FCSTD DOCUMENT  (FreeCAD 0.20R29177 +426 (Git))
Label: ASM_ExtensionHead
License: All rights reserved
LicenseURL: http://en.wikipedia.org/wiki/All_rights_reserved
objects: App::Link×6, App::DocumentObjectGroup×3, PartDesign::CoordinateSystem×1, App::FeaturePython×1, App::Part×1
note: 1 computed .brp shape members not serialized (recipe doc carries the construction recipe); baked Part::Feature solids carry a one-line shape summary decoded from their .brp
EXTERNAL_REF file=EndStopTip.FCStd obj=LCS_Origin
EXTERNAL_REF file=EndStopTip.FCStd obj=Assembly
EXTERNAL_REF file=BreakawayMagnet.FCStd obj=LCS_Origin
EXTERNAL_REF file=EndStopTip.FCStd obj=Variables
EXTERNAL_REF file=BreakawayMagnet.FCStd obj=Assembly
EXTERNAL_REF file=BreakawayHeadBase.FCStd obj=LCS_Origin
EXTERNAL_REF file=EndStopTip.FCStd obj=Pad
EXTERNAL_REF file=EndStopTip.FCStd obj=Pad001
EXTERNAL_REF file=BreakawayHeadBase.FCStd obj=Assembly
EXTERNAL_REF file=ASM_TrussPulley.FCStd obj=LCS_Origin
EXTERNAL_REF file=BreakawayHeadBase.FCStd obj=Sketch002
EXTERNAL_REF file=BreakawayHeadTruss.FCStd obj=Variables
EXTERNAL_REF file=ASM_TrussPulley.FCStd obj=Assembly
EXTERNAL_REF file=HeadTetherMountClip.FCStd obj=LCS_Origin
EXTERNAL_REF file=HeadTetherMountClip.FCStd obj=Assembly

FEATURE [App::DocumentObjectGroup] Parts
FEATURE [PartDesign::CoordinateSystem] LCS_Origin
  AttacherType = Attacher::AttachEngine3D
  MapMode = 2
  Support = -> [X_Axis]
FEATURE [App::FeaturePython] Variables  # WARN: FeaturePython — macro-defined, semantics opaque (R4)
  Type = App::PropertyContainer
FEATURE [App::DocumentObjectGroup] Constraints
FEATURE [App::DocumentObjectGroup] Configurations
FEATURE [App::Link] EndStopTip
  AttachedBy = #LCS_Origin
  AttachedTo = Parent Assembly#LCS_Origin
  AttachmentOffset = pos=(0,0,0) rot=(0,-0.707107,-0.707107;3.14159rad)
  LinkPlacement = pos=(0,0,0) rot=(0,-0.707107,-0.707107;3.14159rad)
  LinkedObject = -> <external EndStopTip.FCStd>#Assembly
  Placement = pos=(0,0,0) rot=(0,-0.707107,-0.707107;3.14159rad)
  SolverId = Asm4EE
  expr: Placement = LCS_Origin.Placement * AttachmentOffset * EndStopTip#LCS_Origin.Placement ^ -1
FEATURE [App::Link] BreakawayMagnet  label="BreakawayMagnetTop"
  AttachedBy = #LCS_Origin
  AttachedTo = EndStopTip#LCS_Origin
  AttachmentOffset = pos=(0,-10,5) rot=(0,0,1;0rad)
  LinkPlacement = pos=(-1.3e-15,5,-10) rot=(0,-0.707107,-0.707107;3.14159rad)
  LinkedObject = -> <external BreakawayMagnet.FCStd>#Assembly
  Placement = pos=(-1.3e-15,5,-10) rot=(0,-0.707107,-0.707107;3.14159rad)
  SolverId = Asm4EE
  expr: .AttachmentOffset.Base.z = <<EndStopTip>>#<<Variables>>.BaseHeight
  expr: Placement = EndStopTip.Placement * EndStopTip#LCS_Origin.Placement * AttachmentOffset * BreakawayMagnet#LCS_Origin.Placement ^ -1
FEATURE [App::Link] BreakawayMagnet001  label="BreakawayMagnetBottom"
  AttachedBy = #LCS_Origin
  AttachedTo = EndStopTip#LCS_Origin
  AttachmentOffset = pos=(0,10,5) rot=(0,0,1;0rad)
  LinkPlacement = pos=(4e-16,5,10) rot=(0,-0.707107,-0.707107;3.14159rad)
  LinkedObject = -> <external BreakawayMagnet.FCStd>#Assembly
  Placement = pos=(4e-16,5,10) rot=(0,-0.707107,-0.707107;3.14159rad)
  SolverId = Asm4EE
  expr: .AttachmentOffset.Base.z = <<EndStopTip>>#<<Variables>>.BaseHeight
  expr: Placement = EndStopTip.Placement * EndStopTip#LCS_Origin.Placement * AttachmentOffset * BreakawayMagnet#LCS_Origin.Placement ^ -1
FEATURE [App::Link] BreakawayHeadBase
  AttachedBy = #LCS_Origin
  AttachedTo = EndStopTip#LCS_Origin
  AttachmentOffset = pos=(0,0,10) rot=(0,-0.707107,0.707107;3.14159rad)
  LinkPlacement = pos=(-9e-16,10,-2.2e-15) rot=(-1,0,0;3.14159rad)
  LinkedObject = -> <external BreakawayHeadBase.FCStd>#Assembly
  Placement = pos=(-9e-16,10,-2.2e-15) rot=(-1,0,0;3.14159rad)
  SolverId = Asm4EE
  expr: .AttachmentOffset.Base.z = <<EndStopTip>>#<<Pad>>.Length + <<EndStopTip>>#<<MagnetPad>>.Length
  expr: Placement = EndStopTip.Placement * EndStopTip#LCS_Origin.Placement * AttachmentOffset * BreakawayHeadBase#LCS_Origin.Placement ^ -1
FEATURE [App::Link] ASM_TrussPulley
  AttachedBy = #LCS_Origin
  AttachedTo = BreakawayHeadBase#LCS_Origin
  AttachmentOffset = pos=(0,-18,-16) rot=(1,0,0;3.40339rad)
  LinkPlacement = pos=(-4e-15,28,16) rot=(1,0,0;0.261799rad)
  LinkedObject = -> <external ASM_TrussPulley.FCStd>#Assembly
  Placement = pos=(-4e-15,28,16) rot=(1,0,0;0.261799rad)
  SolverId = Asm4EE
  expr: .AttachmentOffset.Base.y = <<BreakawayHeadBase>>#<<Sketch002>>.Constraints.HolesOffset * -1
  expr: .AttachmentOffset.Base.z = <<BreakawayHeadBase>>#<<Sketch002>>.Constraints.TrussHoleSpacing / -2
  expr: .AttachmentOffset.Rotation.Angle = 180 + <<BreakawayHeadTruss>>#<<Variables>>.TrussAngle
  expr: Placement = BreakawayHeadBase.Placement * BreakawayHeadBase#LCS_Origin.Placement * AttachmentOffset * ASM_TrussPulley#LCS_Origin.Placement ^ -1
FEATURE [App::Link] HeadTetherMountClip
  AttachedBy = #LCS_Origin
  AttachedTo = Parent Assembly#LCS_Origin
  AttachmentOffset = pos=(10,-18,-10) rot=(0.57735,0.57735,0.57735;2.0944rad)
  LinkPlacement = pos=(10,-18,-10) rot=(0.57735,0.57735,0.57735;2.0944rad)
  LinkedObject = -> <external HeadTetherMountClip.FCStd>#Assembly
  Placement = pos=(10,-18,-10) rot=(0.57735,0.57735,0.57735;2.0944rad)
  SolverId = Asm4EE
  expr: Placement = LCS_Origin.Placement * AttachmentOffset * HeadTetherMountClip#LCS_Origin.Placement ^ -1
FEATURE [App::Part] Assembly
  AssemblyType = Part::Link
  Group = -> [LCS_Origin,Variables,Constraints,Configurations,EndStopTip,BreakawayMagnet,BreakawayMagnet001,BreakawayHeadBase,ASM_TrussPulley,HeadTetherMountClip]
  Origin = -> Origin
  Type = Assembly

RESOLVED EXTERNAL PARTS (link-assembly join: the EXTERNAL_REF files above that resolve inside this repo's crawl, each included once):
---- part ASM_TrussPulley.FCStd = doc fcstd_1721cb35d806 ----
FCSTD DOCUMENT  (FreeCAD 0.20R29177 +426 (Git))
Label: ASM_TrussPulley
License: All rights reserved
LicenseURL: http://en.wikipedia.org/wiki/All_rights_reserved
objects: App::Link×7, App::DocumentObjectGroup×3, PartDesign::CoordinateSystem×2, App::FeaturePython×1, App::Part×1
note: 2 computed .brp shape members not serialized (recipe doc carries the construction recipe); baked Part::Feature solids carry a one-line shape summary decoded from their .brp
EXTERNAL_REF file=BreakawayHeadBase.FCStd obj=Sketch
EXTERNAL_REF file=BreakawayHeadTruss.FCStd obj=LCS_Origin
EXTERNAL_REF file=BreakawayHeadTruss.FCStd obj=Assembly
EXTERNAL_REF file=BreakawayHeadTruss.FCStd obj=Pad
EXTERNAL_REF file=BreakawayHeadTruss.FCStd obj=Sketch
EXTERNAL_REF file=CablePulley.FCStd obj=LCS_Origin
EXTERNAL_REF file=CablePulley.FCStd obj=Assembly
EXTERNAL_REF file=Bearing608.FCStd obj=LCS_axle
EXTERNAL_REF file=Bearing608.FCStd obj=Part
EXTERNAL_REF file=CablePulleyBearingHub.FCStd obj=LCS_Origin
EXTERNAL_REF file=CablePulleyBearingHub.FCStd obj=Assembly

FEATURE [App::DocumentObjectGroup] Parts
FEATURE [PartDesign::CoordinateSystem] LCS_Origin
  AttacherType = Attacher::AttachEngine3D
  MapMode = 2
  Support = -> [X_Axis]
FEATURE [App::FeaturePython] Variables  # WARN: FeaturePython — macro-defined, semantics opaque (R4)
  Type = App::PropertyContainer
FEATURE [App::DocumentObjectGroup] Constraints
FEATURE [App::DocumentObjectGroup] Configurations
FEATURE [App::Link] BreakawayHeadTruss
  AttachedBy = #LCS_Origin
  AttachedTo = Parent Assembly#LCS_Origin
  AttachmentOffset = pos=(8,0,0) rot=(0.57735,0.57735,0.57735;2.0944rad)
  LinkPlacement = pos=(8,0,0) rot=(0.57735,0.57735,0.57735;2.0944rad)
  LinkedObject = -> <external BreakawayHeadTruss.FCStd>#Assembly
  Placement = pos=(8,0,0) rot=(0.57735,0.57735,0.57735;2.0944rad)
  SolverId = Asm4EE
  expr: .AttachmentOffset.Base.x = <<BreakawayHeadBase>>#<<Sketch>>.Constraints.EndWidth / 2
  expr: Placement = LCS_Origin.Placement * AttachmentOffset * BreakawayHeadTruss#LCS_Origin.Placement ^ -1
FEATURE [App::Link] BreakawayHeadTruss001
  AttachedBy = #LCS_Origin
  AttachedTo = Parent Assembly#LCS_Origin
  AttachmentOffset = pos=(-10,0,0) rot=(0.57735,0.57735,0.57735;2.0944rad)
  LinkPlacement = pos=(-10,0,0) rot=(0.57735,0.57735,0.57735;2.0944rad)
  LinkedObject = -> <external BreakawayHeadTruss.FCStd>#Assembly
  Placement = pos=(-10,0,0) rot=(0.57735,0.57735,0.57735;2.0944rad)
  SolverId = Asm4EE
  expr: .AttachmentOffset.Base.x = (<<BreakawayHeadBase>>#<<Sketch>>.Constraints.EndWidth / 2 + <<BreakawayHeadTruss>>#<<Pad>>.Length) * -1
  expr: Placement = LCS_Origin.Placement * AttachmentOffset * BreakawayHeadTruss#LCS_Origin.Placement ^ -1
FEATURE [PartDesign::CoordinateSystem] LCS_Pulley
  AttacherType = Attacher::AttachEngine3D
  AttachmentOffset = pos=(0,180,-29.9096) rot=(0,0,1;0rad)
  MapMode = 2
  Placement = pos=(0,180,-29.9096) rot=(0,0,1;0rad)
  Support = -> [LCS_Origin]
  expr: .AttachmentOffset.Base.y = BreakawayHeadTruss#Sketch.Constraints.TrussLength
  expr: .AttachmentOffset.Base.z = BreakawayHeadTruss#Sketch.Constraints.PulleyHoleOffset * -1
FEATURE [App::Link] CablePulley
  AttachedBy = #LCS_Origin
  AttachedTo = Parent Assembly#LCS_Pulley
  AttachmentOffset = pos=(0,0,0) rot=(0,1,0;1.5708rad)
  LinkPlacement = pos=(0,180,-29.9096) rot=(0,1,0;1.5708rad)
  LinkedObject = -> <external CablePulley.FCStd>#Assembly
  Placement = pos=(0,180,-29.9096) rot=(0,1,0;1.5708rad)
  SolverId = Asm4EE
  expr: Placement = LCS_Pulley.Placement * AttachmentOffset * CablePulley#LCS_Origin.Placement ^ -1
FEATURE [App::Link] PulleyBearing
  AssemblyType = Part::Link
  AttachedBy = #LCS_axle
  AttachedTo = Parent Assembly#LCS_Pulley
  AttachmentOffset = pos=(0,0,0) rot=(0,1,0;1.5708rad)
  LinkPlacement = pos=(0,180,-29.9096) rot=(0,1,0;1.5708rad)
  LinkedObject = -> <external Bearing608.FCStd>#Part
  Placement = pos=(0,180,-29.9096) rot=(0,1,0;1.5708rad)
  SolverId = Asm4EE
  expr: Placement = LCS_Pulley.Placement * AttachmentOffset * Bearing608#LCS_axle.Placement ^ -1
FEATURE [App::Link] CablePulleyBearingHub001
  AttachedBy = #LCS_Origin
  AttachedTo = Parent Assembly#LCS_Pulley
  AttachmentOffset = pos=(3.5,0,0) rot=(0,1,0;4.71239rad)
  LinkPlacement = pos=(3.5,180,-29.9096) rot=(0,1,0;4.71239rad)
  LinkedObject = -> <external CablePulleyBearingHub.FCStd>#Assembly
  Placement = pos=(3.5,180,-29.9096) rot=(0,1,0;4.71239rad)
  SolverId = Asm4EE
  expr: Placement = LCS_Pulley.Placement * AttachmentOffset * CablePulleyBearingHub#LCS_Origin.Placement ^ -1
FEATURE [App::Link] CablePulleyBearingHub002
  AttachedBy = #LCS_Origin
  AttachedTo = Parent Assembly#LCS_Pulley
  AttachmentOffset = pos=(-3.5,0,0) rot=(-0.707107,0,-0.707107;3.14159rad)
  LinkPlacement = pos=(-3.5,180,-29.9096) rot=(-0.707107,0,-0.707107;3.14159rad)
  LinkedObject = -> <external CablePulleyBearingHub.FCStd>#Assembly
  Placement = pos=(-3.5,180,-29.9096) rot=(-0.707107,0,-0.707107;3.14159rad)
  SolverId = Asm4EE
  expr: Placement = LCS_Pulley.Placement * AttachmentOffset * CablePulleyBearingHub#LCS_Origin.Placement ^ -1
FEATURE [App::Link] CablePulley001
  AttachedBy = #LCS_Origin
  AttachedTo = Parent Assembly#LCS_Pulley
  AttachmentOffset = pos=(0,0,0) rot=(0,1,0;-1.5708rad)
  LinkPlacement = pos=(0,180,-29.9096) rot=(0,1,0;4.71239rad)
  LinkedObject = -> <external CablePulley.FCStd>#Assembly
  Placement = pos=(0,180,-29.9096) rot=(0,1,0;4.71239rad)
  SolverId = Asm4EE
  expr: Placement = LCS_Pulley.Placement * AttachmentOffset * CablePulley#LCS_Origin.Placement ^ -1
FEATURE [App::Part] Assembly
  AssemblyType = Part::Link
  Group = -> [LCS_Origin,Variables,Constraints,Configurations,BreakawayHeadTruss,BreakawayHeadTruss001,LCS_Pulley,CablePulley,PulleyBearing,CablePulleyBearingHub001,CablePulleyBearingHub002,CablePulley001]
  Origin = -> Origin
  Type = Assembly
---- part BreakawayHeadBase.FCStd = doc fcstd_181b5c8611f0 ----
FCSTD DOCUMENT  (FreeCAD 0.20R29177 +426 (Git))
Label: BreakawayHeadBase
License: All rights reserved
LicenseURL: http://en.wikipedia.org/wiki/All_rights_reserved
objects: Sketcher::SketchObject×5, App::DocumentObjectGroup×4, PartDesign::Pocket×4, Part::FeaturePython×4, PartDesign::CoordinateSystem×2, App::Link×2, App::FeaturePython×1, PartDesign::Pad×1, PartDesign::Body×1, App::Part×1
note: 22 computed .brp shape members not serialized (recipe doc carries the construction recipe); baked Part::Feature solids carry a one-line shape summary decoded from their .brp
EXTERNAL_REF file=EndStopTip.FCStd obj=Sketch003
EXTERNAL_REF file=EndStopTip.FCStd obj=Sketch
EXTERNAL_REF file=BreakawayMagnet.FCStd obj=LCS_Origin
EXTERNAL_REF file=BreakawayMagnet.FCStd obj=Assembly

FEATURE [App::DocumentObjectGroup] Parts
FEATURE [PartDesign::CoordinateSystem] LCS_Origin
  AttacherType = Attacher::AttachEngine3D
  MapMode = 2
  Support = -> [X_Axis]
FEATURE [App::FeaturePython] Variables  # WARN: FeaturePython — macro-defined, semantics opaque (R4)
  Type = App::PropertyContainer
FEATURE [App::DocumentObjectGroup] Constraints
FEATURE [App::DocumentObjectGroup] Configurations
FEATURE [Sketcher::SketchObject] Sketch
  FullyConstrained = true
  MapMode = 5
  Support = -> [XY_Plane001]
  expr: Constraints[9] = <<EndStopTip>>#<<SketchChamfer>>.Constraints.MateWidth
  sketch-geometry (14):
    g0: ArcOfCircle CenterX=-10.567 CenterY=-0.5 CenterZ=0 NormalX=0 NormalY=0 NormalZ=1 AngleXU=0 Radius=0.5 StartAngle=1.5708 EndAngle=3.66519
    g1: LineSegment StartX=-10.567 StartY=0 StartZ=0 EndX=10.567 EndY=0 EndZ=0
    g2: ArcOfCircle CenterX=10.567 CenterY=-0.5 CenterZ=0 NormalX=0 NormalY=0 NormalZ=1 AngleXU=0 Radius=0.5 StartAngle=5.75959 EndAngle=7.85398
    g3: LineSegment StartX=11 StartY=-0.75 StartZ=0 EndX=8 EndY=-5.94615 EndZ=0
    g4: LineSegment StartX=-8 StartY=-5.94615 StartZ=0 EndX=-11 EndY=-0.75 EndZ=0
    g5: GeomPoint X=-11.433 Y=0 Z=0
    g6: LineSegment StartX=-8 StartY=-5.94615 StartZ=0 EndX=-8 EndY=-23 EndZ=0
    g7: LineSegment StartX=-7 StartY=-24 StartZ=0 EndX=7 EndY=-24 EndZ=0
    g8: LineSegment StartX=8 StartY=-23 StartZ=0 EndX=8 EndY=-5.94615 EndZ=0
    g9: GeomPoint X=0 Y=-24 Z=0
    g10: ArcOfCircle CenterX=7 CenterY=-23 CenterZ=0 NormalX=0 NormalY=0 NormalZ=1 AngleXU=0 Radius=1 StartAngle=4.71239 EndAngle=6.28319
    g11: GeomPoint X=8 Y=-24 Z=0
    g12: ArcOfCircle CenterX=-7 CenterY=-23 CenterZ=0 NormalX=0 NormalY=0 NormalZ=1 AngleXU=0 Radius=1 StartAngle=3.14159 EndAngle=4.71239
    g13: GeomPoint X=-8 Y=-24 Z=0
  constraints (32):
    c: Tangent(g0,g1) = 1.5708
    c: Tangent(g1,g2) = 1.5708
    c: Tangent(g2,g3) = 1.5708
    c: Tangent(g4,g0) = 1.5708
    c: Horizontal(g1)
    c: Equal(g0,g2)
    c: PointOnObject(g5,g1)
    c: PointOnObject(g5,g4)
    c: Radius(g0) = 0.5
    c: DistanceX(g0,g2) = 22
    c: Symmetric(g1,g0,g-1)
    c: Vertical(g6)
    c: Horizontal(g7)
    c: Vertical(g8)
    c: Symmetric(g13,g11,g9)
    c: PointOnObject(g9,g-2)
    c: Coincident(g4,g6)
    c: Coincident(g8,g3)
    c: Equal(g4,g3)
    c: Angle(g1,g3) = 1.0472
    c: DistanceX(g13,g11) = 16  'EndWidth'
    c: DistanceY(g11,g-1) = 24  'Length'
    c: PointOnObject(g11,g8)
    c: PointOnObject(g11,g7)
    c: Tangent(g8,g10) = -1.5708
    c: Tangent(g7,g10) = -1.5708
    c: PointOnObject(g13,g7)
    c: PointOnObject(g13,g6)
    c: Tangent(g7,g12) = -1.5708
    c: Tangent(g6,g12) = -1.5708
    c: Equal(g12,g10)
    c: Radius(g10) = 1
FEATURE [PartDesign::Pad] Pad
  Direction = (0,0,1)
  Length = 42
  Length2 = 10
  Midplane = true
  Profile = -> Sketch
  ReferenceAxis = -> Sketch [N_Axis]
  Type = 0
  expr: Length = <<EndStopTip>>#<<Sketch>>.Constraints.Height
FEATURE [Sketcher::SketchObject] Sketch001
  FullyConstrained = true
  MapMode = 5
  Placement = pos=(0,0,0) rot=(0.57735,0.57735,0.57735;2.0944rad)
  Support = -> [YZ_Plane001]
  expr: Constraints[25] = <<Sketch>>.Constraints.Length
  sketch-geometry (9):
    g0: LineSegment StartX=-24 StartY=13 StartZ=0 EndX=-34.7696 EndY=13 EndZ=0
    g1: LineSegment StartX=-34.7696 StartY=13 StartZ=0 EndX=-42.3848 EndY=5.38478 EndZ=0
    g2: LineSegment StartX=-42.3848 StartY=5.38478 StartZ=0 EndX=-42.3848 EndY=-5.38478 EndZ=0
    g3: LineSegment StartX=-42.3848 StartY=-5.38478 StartZ=0 EndX=-34.7696 EndY=-13 EndZ=0
    g4: LineSegment StartX=-34.7696 StartY=-13 StartZ=0 EndX=-24 EndY=-13 EndZ=0
    g5: LineSegment StartX=-24 StartY=-13 StartZ=0 EndX=-16.3848 EndY=-5.38478 EndZ=0
    g6: LineSegment StartX=-16.3848 StartY=-5.38478 StartZ=0 EndX=-16.3848 EndY=5.38478 EndZ=0
    g7: LineSegment StartX=-16.3848 StartY=5.38478 StartZ=0 EndX=-24 EndY=13 EndZ=0
    g8: Circle CenterX=-29.3848 CenterY=0 CenterZ=0 NormalX=0 NormalY=0 NormalZ=1 AngleXU=0 Radius=14.0711
  constraints (21):
    c: Coincident(g0,g1)
    c: Coincident(g1,g2)
    c: Coincident(g2,g3)
    c: Coincident(g3,g4)
    c: Coincident(g4,g5)
    c: Coincident(g5,g6)
    c: Coincident(g6,g7)
    c: Coincident(g7,g0)
    c: Equal(g0, g1-g7) x7
    c: PointOnObject(g0,g8)
    c: PointOnObject(g1,g8)
    c: PointOnObject(g2,g8)
    c: PointOnObject(g3,g8)
    c: PointOnObject(g4,g8)
    c: PointOnObject(g5,g8)
    c: PointOnObject(g6,g8)
    c: PointOnObject(g7,g8)
    c: PointOnObject(g8,g-1)
    c: Horizontal(g0)
    c: DistanceX(g4,g-1) = 24
    c: DistanceY(g3,g0) = 26
FEATURE [PartDesign::Pocket] Pocket  label="Cutout"
  BaseFeature = -> Pad
  Direction = (-1,2e-16,-3e-16)
  Length = 5
  Length2 = 5
  Midplane = true
  Profile = -> Sketch001
  ReferenceAxis = -> Sketch001 [N_Axis]
  Type = 1
FEATURE [Sketcher::SketchObject] Sketch002
  FullyConstrained = true
  MapMode = 5
  Placement = pos=(0,0,0) rot=(0.57735,0.57735,0.57735;2.0944rad)
  Support = -> [YZ_Plane001]
  expr: .Constraints.HolesOffset = <<Sketch>>.Constraints.Length - 6mm
  expr: .Constraints.TrussHoleSpacing = <<Pad>>.Length - 10mm
  sketch-geometry (12):
    g0: LineSegment StartX=-18 StartY=16 StartZ=0 EndX=-18 EndY=-16 EndZ=0
    g1: GeomPoint X=-18 Y=0 Z=0
    g2: ArcOfCircle CenterX=-18 CenterY=16 CenterZ=0 NormalX=0 NormalY=0 NormalZ=1 AngleXU=0 Radius=2.15 StartAngle=2.35619 EndAngle=7.06858
    g3: LineSegment StartX=-19.5203 StartY=17.5203 StartZ=0 EndX=-18.8906 EndY=18.15 EndZ=0
    g4: LineSegment StartX=-16.4797 StartY=17.5203 StartZ=0 EndX=-17.1094 EndY=18.15 EndZ=0
    g5: LineSegment StartX=-17.1094 StartY=18.15 StartZ=0 EndX=-18.8906 EndY=18.15 EndZ=0
    g6: ArcOfCircle CenterX=-18 CenterY=16 CenterZ=0 NormalX=0 NormalY=0 NormalZ=1 AngleXU=0 Radius=2.15 StartAngle=0.785398 EndAngle=2.35619
    g7: ArcOfCircle CenterX=-18 CenterY=-16 CenterZ=0 NormalX=0 NormalY=0 NormalZ=1 AngleXU=0 Radius=2.15 StartAngle=2.35619 EndAngle=7.06858
    g8: LineSegment StartX=-19.5203 StartY=-14.4797 StartZ=0 EndX=-18.8906 EndY=-13.85 EndZ=0
    g9: LineSegment StartX=-16.4797 StartY=-14.4797 StartZ=0 EndX=-17.1094 EndY=-13.85 EndZ=0
    g10: LineSegment StartX=-17.1094 StartY=-13.85 StartZ=0 EndX=-18.8906 EndY=-13.85 EndZ=0
    g11: ArcOfCircle CenterX=-18 CenterY=-16 CenterZ=0 NormalX=0 NormalY=0 NormalZ=1 AngleXU=0 Radius=2.15 StartAngle=0.785398 EndAngle=2.35619
  constraints (31):
    c: Vertical(g0)
    c: PointOnObject(g1,g-1)
    c: DistanceY(g0,g0) = 32  'TrussHoleSpacing'
    c: DistanceX(g1,g-1) = 18  'HolesOffset'
    c: Coincident(g2,g0)
    c: Symmetric(g2,g0,g1)
    c: Coincident(g5,g4)
    c: Coincident(g5,g3)
    c: Horizontal(g5)
    c: Tangent(g4,g2) = -1.5708
    c: Tangent(g3,g2) = 1.5708
    c: Diameter(g2) = 4.3
    c: Coincident(g6,g2)
    c: Coincident(g6,g2)
    c: Coincident(g6,g2)
    c: Tangent(g5,g6)
    c: Equal(g4,g3)
    c: Angle(g5,g4) = 2.35619
    c: Coincident(g10,g9)
    c: Coincident(g10,g8)
    c: Horizontal(g10)
    c: Tangent(g9,g7) = -1.5708
    c: Tangent(g8,g7) = 1.5708
    c: Equal(g2,g7) = 5.4
    c: Coincident(g11,g7)
    c: Coincident(g11,g7)
    c: Coincident(g11,g7)
    c: Tangent(g10,g11)
    c: Equal(g9,g8)
    c: Angle(g10,g9) = 2.35619
    c: Coincident(g7,g0)
FEATURE [PartDesign::Pocket] Pocket001  label="TrussHoles"
  BaseFeature = -> Pocket
  Direction = (-1,2e-16,-3e-16)
  Length = 5
  Length2 = 5
  Midplane = true
  Profile = -> Sketch002
  ReferenceAxis = -> Sketch002 [N_Axis]
  Type = 1
FEATURE [Sketcher::SketchObject] Sketch003
  FullyConstrained = true
  MapMode = 5
  Placement = pos=(0,0,0) rot=(1,0,0;1.5708rad)
  Support = -> [XZ_Plane001]
  sketch-geometry (13):
    g0: ArcOfCircle CenterX=0 CenterY=10 CenterZ=0 NormalX=0 NormalY=0 NormalZ=1 AngleXU=0 Radius=9.25 StartAngle=2.35619 EndAngle=3.92699
    g1: ArcOfCircle CenterX=0 CenterY=10 CenterZ=0 NormalX=0 NormalY=0 NormalZ=1 AngleXU=0 Radius=9.25 StartAngle=5.49779 EndAngle=7.06858
    g2: ArcOfCircle CenterX=-9e-16 CenterY=-10 CenterZ=0 NormalX=0 NormalY=0 NormalZ=1 AngleXU=0 Radius=9.25 StartAngle=5.49779 EndAngle=7.06858
    g3: ArcOfCircle CenterX=-9e-16 CenterY=-10 CenterZ=0 NormalX=0 NormalY=0 NormalZ=1 AngleXU=0 Radius=9.25 StartAngle=2.35619 EndAngle=3.92699
    g4: LineSegment StartX=-6.54074 StartY=3.45926 StartZ=0 EndX=-6.54074 EndY=-3.45926 EndZ=0
    g5: LineSegment StartX=6.54074 StartY=3.45926 StartZ=0 EndX=6.54074 EndY=-3.45926 EndZ=0
    g6: LineSegment StartX=6.54074 StartY=-16.5407 StartZ=0 EndX=6.54074 EndY=-22.5407 EndZ=0
    g7: LineSegment StartX=6.54074 StartY=-22.5407 StartZ=0 EndX=-6.54074 EndY=-22.5407 EndZ=0
    g8: LineSegment StartX=-6.54074 StartY=-22.5407 StartZ=0 EndX=-6.54074 EndY=-16.5407 EndZ=0
    g9: LineSegment StartX=-6.54074 StartY=16.5407 StartZ=0 EndX=-6.54074 EndY=22.5407 EndZ=0
    g10: LineSegment StartX=-6.54074 StartY=22.5407 StartZ=0 EndX=6.54074 EndY=22.5407 EndZ=0
    g11: LineSegment StartX=6.54074 StartY=22.5407 StartZ=0 EndX=6.54074 EndY=16.5407 EndZ=0
    g12: LineSegment StartX=-6.54074 StartY=-3.45926 StartZ=0 EndX=-3.08148 EndY=0 EndZ=0
  constraints (39):
    c: PointOnObject(g1,g-2)
    c: Symmetric(g1,g3,g-1)
    c: DistanceY(g3,g1) = 20
    c: Coincident(g1,g0)
    c: Diameter(g1) = 18.5
    c: Coincident(g3,g2)
    c: Coincident(g4,g0)
    c: Coincident(g4,g3)
    c: Coincident(g5,g1)
    c: Coincident(g5,g2)
    c: Coincident(g6,g2)
    c: Vertical(g6)
    c: Coincident(g7,g6)
    c: Horizontal(g7)
    c: Coincident(g8,g3)
    c: Vertical(g8)
    c: Coincident(g9,g0)
    c: Vertical(g9)
    c: Coincident(g10,g9)
    c: Horizontal(g10)
    c: Coincident(g11,g10)
    c: Coincident(g11,g1)
    c: Vertical(g11)
    c: Vertical(g5)
    c: Vertical(g4)
    c: Equal(g0,g1)
    c: Equal(g2,g3)
    c: Equal(g2,g1)
    c: Equal(g6,g8)
    c: Coincident(g8,g7)
    c: Equal(g9,g11)
    c: Equal(g10,g7)
    c: PointOnObject(g2,g6)
    c: PointOnObject(g3,g8)
    c: PointOnObject(g12,g-1)
    c: Tangent(g12,g3) = 1.5708
    c: Angle(g12,g-1) = 2.35619
    c: DistanceY(g11,g11) = 6
    c: Equal(g6,g11)
FEATURE [PartDesign::Pocket] Pocket002  label="MagnetHoles"
  BaseFeature = -> Pocket001
  Direction = (0,1,2e-16)
  Length = 1.5
  Length2 = 5
  Profile = -> Sketch003
  ReferenceAxis = -> Sketch003 [N_Axis]
  Reversed = true
  Type = 0
FEATURE [Sketcher::SketchObject] Sketch004
  FullyConstrained = true
  MapMode = 5
  Placement = pos=(0,0,0) rot=(1,0,0;1.5708rad)
  Support = -> [XZ_Plane001]
  sketch-geometry (8):
    g0: ArcOfCircle CenterX=0 CenterY=10 CenterZ=0 NormalX=0 NormalY=0 NormalZ=1 AngleXU=0 Radius=2.25 StartAngle=2.35619 EndAngle=7.06858
    g1: LineSegment StartX=-1.59099 StartY=11.591 StartZ=0 EndX=-0.931981 EndY=12.25 EndZ=0
    g2: LineSegment StartX=-0.931981 StartY=12.25 StartZ=0 EndX=0.931981 EndY=12.25 EndZ=0
    g3: LineSegment StartX=0.931981 StartY=12.25 StartZ=0 EndX=1.59099 EndY=11.591 EndZ=0
    g4: ArcOfCircle CenterX=0 CenterY=-10 CenterZ=0 NormalX=0 NormalY=0 NormalZ=1 AngleXU=0 Radius=2.25 StartAngle=2.35619 EndAngle=7.06858
    g5: LineSegment StartX=-1.59099 StartY=-8.40901 StartZ=0 EndX=-0.931981 EndY=-7.75 EndZ=0
    g6: LineSegment StartX=-0.931981 StartY=-7.75 StartZ=0 EndX=0.931981 EndY=-7.75 EndZ=0
    g7: LineSegment StartX=0.931981 StartY=-7.75 StartZ=0 EndX=1.59099 EndY=-8.40901 EndZ=0
  constraints (21):
    c: PointOnObject(g0,g-2)
    c: Coincident(g2,g1)
    c: Horizontal(g2)
    c: Coincident(g3,g2)
    c: Tangent(g3,g0) = 1.5708
    c: Tangent(g1,g0) = 1.5708
    c: Equal(g1,g3)
    c: Angle(g2,g3) = 2.35619
    c: Diameter(g0) = 4.5
    c: Tangent(g2,g0)
    c: Coincident(g6,g5)
    c: Horizontal(g6)
    c: Coincident(g7,g6)
    c: Tangent(g7,g4) = 1.5708
    c: Tangent(g5,g4) = 1.5708
    c: Equal(g5,g7)
    c: Angle(g6,g7) = 2.35619
    c: Equal(g0,g4) = 4.5
    c: Tangent(g6,g4)
    c: Symmetric(g4,g0,g-1)
    c: DistanceY(g4,g0) = 20
FEATURE [PartDesign::Pocket] Pocket003  label="MagnetMountHoles"
  BaseFeature = -> Pocket002
  Direction = (0,1,2e-16)
  Length = 16
  Length2 = 5
  Profile = -> Sketch004
  ReferenceAxis = -> Sketch004 [N_Axis]
  Reversed = true
  Type = 0
FEATURE [PartDesign::Body] Body
  Group = -> [Sketch,Pad,Sketch001,Pocket,Sketch002,Pocket001,Sketch003,Pocket002,Sketch004,Pocket003]
  Origin = -> Origin001
  Tip = -> Pocket003
FEATURE [App::Link] BreakawayMagnetTop
  AttachedBy = #LCS_Origin
  AttachedTo = Parent Assembly#LCS_Origin
  AttachmentOffset = pos=(0,-1.5,10) rot=(1,0,0;4.71239rad)
  LinkPlacement = pos=(0,-1.5,10) rot=(1,0,0;4.71239rad)
  LinkedObject = -> <external BreakawayMagnet.FCStd>#Assembly
  Placement = pos=(0,-1.5,10) rot=(1,0,0;4.71239rad)
  SolverId = Asm4EE
  expr: .AttachmentOffset.Base.y = <<MagnetHoles>>.Length * -1
  expr: Placement = LCS_Origin.Placement * AttachmentOffset * BreakawayMagnet#LCS_Origin.Placement ^ -1
FEATURE [App::Link] BreakawayMagnetTop001  label="BreakawayMagnetBottom"
  AttachedBy = #LCS_Origin
  AttachedTo = Parent Assembly#LCS_Origin
  AttachmentOffset = pos=(0,-1.5,-10) rot=(1,0,0;4.71239rad)
  LinkPlacement = pos=(0,-1.5,-10) rot=(1,0,0;4.71239rad)
  LinkedObject = -> <external BreakawayMagnet.FCStd>#Assembly
  Placement = pos=(0,-1.5,-10) rot=(1,0,0;4.71239rad)
  SolverId = Asm4EE
  expr: .AttachmentOffset.Base.y = <<MagnetHoles>>.Length * -1
  expr: Placement = LCS_Origin.Placement * AttachmentOffset * BreakawayMagnet#LCS_Origin.Placement ^ -1
FEATURE [PartDesign::CoordinateSystem] LCS_TrussHoles
  AttacherType = Attacher::AttachEngine3D
  AttachmentOffset = pos=(0,-18,0) rot=(0,0,1;0rad)
  MapMode = 2
  Placement = pos=(0,-18,0) rot=(0,0,1;0rad)
  Support = -> [LCS_Origin]
  expr: .AttachmentOffset.Base.y = <<Sketch002>>.Constraints.HolesOffset * -1
FEATURE [Part::FeaturePython] Screw  label="M4x25-Screw"  # Fasteners workbench fastener (typed FeaturePython)
  Placement = pos=(10,-18,-16) rot=(0,1,0;1.5708rad)
  baseObject = -> Body [Edge93]
  diameter = 5
  invert = false
  leftHanded = false
  length = 7
  lengthCustom = 25
  matchOuter = false
  offset = 2
  thread = false
  type = 45
FEATURE [Part::FeaturePython] Screw001  label="M4x25-Screw001"  # Fasteners workbench fastener (typed FeaturePython)
  Placement = pos=(10,-18,16) rot=(0,1,0;1.5708rad)
  baseObject = -> Body [Edge89]
  diameter = 5
  invert = false
  leftHanded = false
  length = 7
  lengthCustom = 25
  matchOuter = false
  offset = 2
  thread = false
  type = 45
FEATURE [Part::FeaturePython] Nut  label="M4-Nut"  # Fasteners workbench fastener (typed FeaturePython)
  Placement = pos=(-9.6,-18,16) rot=(0,-1,0;1.5708rad)
  baseObject = -> Screw001 [Edge35]
  diameter = 2
  invert = true
  leftHanded = false
  matchOuter = true
  offset = -5
  thread = false
  type = 19
FEATURE [Part::FeaturePython] Nut001  label="M4-Nut001"  # Fasteners workbench fastener (typed FeaturePython)
  Placement = pos=(-9.6,-18,-16) rot=(0,-1,0;1.5708rad)
  baseObject = -> Screw [Edge35]
  diameter = 2
  invert = true
  leftHanded = false
  matchOuter = true
  offset = -5
  thread = false
  type = 19
FEATURE [App::DocumentObjectGroup] Fasteners
  Group = -> [Screw,Screw001,Nut,Nut001]
FEATURE [App::Part] Assembly
  AssemblyType = Part::Link
  Group = -> [LCS_Origin,Variables,Constraints,Configurations,Body,BreakawayMagnetTop,BreakawayMagnetTop001,Fasteners,LCS_TrussHoles,Screw,Screw001,Nut,Nut001]
  Origin = -> Origin
  Type = Assembly
---- part BreakawayHeadTruss.FCStd = doc fcstd_5e5b53ead47f ----
FCSTD DOCUMENT  (FreeCAD 0.20R29177 +426 (Git))
Label: BreakawayHeadTruss
License: All rights reserved
LicenseURL: http://en.wikipedia.org/wiki/All_rights_reserved
objects: App::DocumentObjectGroup×3, Sketcher::SketchObject×2, PartDesign::CoordinateSystem×1, App::FeaturePython×1, PartDesign::Pad×1, PartDesign::Pocket×1, PartDesign::LinearPattern×1, PartDesign::Body×1, App::Part×1
note: 9 computed .brp shape members not serialized (recipe doc carries the construction recipe); baked Part::Feature solids carry a one-line shape summary decoded from their .brp
EXTERNAL_REF file=BreakawayHeadBase.FCStd obj=Sketch002

FEATURE [App::DocumentObjectGroup] Parts
FEATURE [PartDesign::CoordinateSystem] LCS_Origin
  AttacherType = Attacher::AttachEngine3D
  MapMode = 2
  Support = -> [X_Axis]
FEATURE [App::FeaturePython] Variables  # WARN: FeaturePython — macro-defined, semantics opaque (R4)
  CompressionWidth = 8
  InternalRadius = 2
  TensionWidth = 4
  TrussAngle = 15
  Type = App::PropertyContainer
FEATURE [App::DocumentObjectGroup] Constraints
FEATURE [App::DocumentObjectGroup] Configurations
FEATURE [Sketcher::SketchObject] Sketch
  FullyConstrained = true
  MapMode = 5
  Support = -> [XY_Plane001]
  expr: Constraints[35] = <<Variables>>.CompressionWidth
  expr: Constraints[38] = <<Variables>>.TensionWidth
  expr: Constraints[50] = <<Variables>>.TensionWidth
  expr: Constraints[51] = <<Variables>>.CompressionWidth
  expr: Constraints[62] = <<BreakawayHeadBase>>#<<Sketch002>>.Constraints.TrussHoleSpacing
  expr: Constraints[65] = 90 - <<Variables>>.TrussAngle
  sketch-geometry (26):
    g0: Circle CenterX=0 CenterY=0 CenterZ=0 NormalX=0 NormalY=0 NormalZ=1 AngleXU=0 Radius=2.15
    g1: ArcOfCircle CenterX=0 CenterY=0 CenterZ=0 NormalX=0 NormalY=0 NormalZ=1 AngleXU=0 Radius=5 StartAngle=1.5708 EndAngle=2.87979
    g2: ArcOfCircle CenterX=180 CenterY=-29.9096 CenterZ=0 NormalX=0 NormalY=0 NormalZ=1 AngleXU=0 Radius=6 StartAngle=4.71239 EndAngle=7.35705
    g3: ArcOfCircle CenterX=-8.28221 CenterY=-30.9096 CenterZ=0 NormalX=0 NormalY=0 NormalZ=1 AngleXU=0 Radius=5 StartAngle=2.87979 EndAngle=4.71239
    g4: LineSegment StartX=-13.1118 StartY=-29.6155 StartZ=0 EndX=-4.82963 EndY=1.2941 EndZ=0
    g5: LineSegment StartX=180 StartY=-35.9096 StartZ=0 EndX=-8.28221 EndY=-35.9096 EndZ=0
    g6: Circle CenterX=180 CenterY=-29.9096 CenterZ=0 NormalX=0 NormalY=0 NormalZ=1 AngleXU=0 Radius=2.15
    g7: ArcOfCircle CenterX=173.149 CenterY=-26.0427 CenterZ=0 NormalX=0 NormalY=0 NormalZ=1 AngleXU=0 Radius=1.86688 StartAngle=4.71239 EndAngle=7.35705
    g8: ArcOfCircle CenterX=180 CenterY=-29.9096 CenterZ=0 NormalX=0 NormalY=0 NormalZ=1 AngleXU=0 Radius=6 StartAngle=1.07386 EndAngle=4.71239
    g9: LineSegment StartX=130 StartY=-25.9096 StartZ=0 EndX=130 EndY=-3.87784 EndZ=0
    g10: ArcOfCircle CenterX=132 CenterY=-25.9096 CenterZ=0 NormalX=0 NormalY=0 NormalZ=1 AngleXU=0 Radius=2 StartAngle=3.14159 EndAngle=4.71239
    g11: ArcOfCircle CenterX=132 CenterY=-3.87784 CenterZ=0 NormalX=0 NormalY=0 NormalZ=1 AngleXU=0 Radius=2 StartAngle=1.07386 EndAngle=3.14159
    g12: LineSegment StartX=132 StartY=-27.9096 StartZ=0 EndX=173.149 EndY=-27.9096 EndZ=0
    g13: LineSegment StartX=132.953 StartY=-2.11974 StartZ=0 EndX=174.039 EndY=-24.4017 EndZ=0
    g14: LineSegment StartX=182.86 StartY=-24.6353 StartZ=0 EndX=130 EndY=4.03238 EndZ=0
    g15: LineSegment StartX=3e-16 StartY=5 StartZ=0 EndX=126.186 EndY=5 EndZ=0
    g16: LineSegment StartX=174.039 StartY=-24.4017 StartZ=0 EndX=175.946 EndY=-20.8855 EndZ=0
    g17: ArcOfCircle CenterX=126.186 CenterY=-3 CenterZ=0 NormalX=0 NormalY=0 NormalZ=1 AngleXU=0 Radius=8 StartAngle=1.07386 EndAngle=1.5708
    g18: GeomPoint X=128.216 Y=5 Z=0
    g19: LineSegment StartX=8 StartY=1 StartZ=0 EndX=130 EndY=1 EndZ=0
    g20: LineSegment StartX=130 StartY=1 StartZ=0 EndX=130 EndY=-27.9096 EndZ=0
    g21: LineSegment StartX=130 StartY=-27.9096 StartZ=0 EndX=8 EndY=-27.9096 EndZ=0
    g22: LineSegment StartX=8 StartY=-27.9096 StartZ=0 EndX=8 EndY=1 EndZ=0
    g23: GeomPoint X=8 Y=-13.4548 Z=0
    g24: LineSegment StartX=0 StartY=0 StartZ=0 EndX=-8.28221 EndY=-30.9096 EndZ=0
    g25: Circle CenterX=-8.28221 CenterY=-30.9096 CenterZ=0 NormalX=0 NormalY=0 NormalZ=1 AngleXU=0 Radius=2.15
  constraints (68):
    c: Diameter(g0) = 4.3
    c: Tangent(g3,g4) = 1.5708
    c: Tangent(g4,g1) = 1.5708
    c: Horizontal(g5)
    c: DistanceX(g-1,g2) = 180  'TrussLength'
    c: Tangent(g5,g3) = 1.5708
    c: Coincident(g6,g2)
    c: Radius(g1) = 5
    c: Coincident(g1,g0)
    c: Radius(g2) = 6
    c: Coincident(g8,g2)
    c: Coincident(g8,g2)
    c: Vertical(g9)
    c: Tangent(g9,g10) = 1.5708
    c: Tangent(g9,g11) = 1.5708
    c: Tangent(g12,g10) = -1.5708
    c: Tangent(g7,g12) = -1.5708
    c: Tangent(g7,g8)
    c: Tangent(g5,g2) = 1.5708
    c: Coincident(g8,g2)
    c: Horizontal(g12)
    c: Tangent(g13,g7) = 1.5708
    c: Tangent(g13,g11) = 1.5708
    c: Tangent(g14,g2) = -1.5708
    c: Horizontal(g15)
    c: Parallel(g14,g13)
    c: Coincident(g16,g7)
    c: PointOnObject(g16,g14)
    c: Perpendicular(g13,g16)
    c: Tangent(g15,g1) = 1.5708
    c: PointOnObject(g18,g15)
    c: PointOnObject(g18,g14)
    c: Tangent(g15,g17) = 1.5708
    c: Tangent(g14,g17) = -1.5708
    c: Radius(g17) = 8
    c: DistanceY(g3,g10) = 8
    c: Equal(g11,g10)
    c: Radius(g10) = 2
    c: Distance(g16) = 4
    c: DistanceX(g9,g2) = 50
    c: PointOnObject(g14,g9)
    c: Coincident(g19,g20)
    c: Coincident(g20,g21)
    c: Coincident(g21,g22)
    c: Coincident(g22,g19)
    c: Horizontal(g19)
    c: Horizontal(g21)
    c: Vertical(g20)
    c: Vertical(g22)
    c: PointOnObject(g20,g12)
    c: DistanceY(g19,g15) = 4
    c: DistanceX(g0,g19) = 8
    c: DistanceX(g19,g19) = 122  'TrussWidth'
    c: DistanceY(g22,g22) = 28.9096  'TrussHeight'
    c: DistanceX(g-1,g21) = 8  'TrussOffsetX'
    c: Symmetric(g19,g21,g23)
    c: DistanceY(g-1,g23) = -13.4548  'TrussOffsetY'
    c: PointOnObject(g20,g9)
    c: DistanceY(g2,g-1) = 29.9096  'PulleyHoleOffset'
    c: Equal(g3,g1)
    c: Coincident(g24,g0)
    c: Coincident(g24,g3)
    c: Distance(g24) = 32
    c: Coincident(g25,g3)
    c: Equal(g25,g0)
    c: Angle(g-1,g24) = 1.309
    c: Coincident(g0,g-1)
    c: Equal(g6,g25)
FEATURE [PartDesign::Pad] Pad
  Direction = (0,0,1)
  Length = 2
  Length2 = 10
  Profile = -> Sketch
  ReferenceAxis = -> Sketch [N_Axis]
  Type = 0
FEATURE [Sketcher::SketchObject] Sketch_1
  FullyConstrained = true
  MapMode = 2
  Support = -> [XY_Plane001]
  expr: Constraints[10] = Sketch.Constraints.TrussOffsetX
  expr: Constraints[11] = Sketch.Constraints.TrussWidth
  expr: Constraints[12] = Sketch.Constraints.TrussHeight
  expr: Constraints[26] = <<Variables>>.TensionWidth
  expr: Constraints[56] = <<Variables>>.InternalRadius
  expr: Constraints[67] = <<Variables>>.CompressionWidth
  expr: Constraints[9] = Sketch.Constraints.TrussOffsetY
  sketch-geometry (31):
    g0: LineSegment StartX=8 StartY=-27.9096 StartZ=0 EndX=8 EndY=1 EndZ=0
    g1: LineSegment StartX=8 StartY=1 StartZ=0 EndX=130 EndY=1 EndZ=0
    g2: LineSegment StartX=130 StartY=1 StartZ=0 EndX=130 EndY=-27.9096 EndZ=0
    g3: LineSegment StartX=130 StartY=-27.9096 StartZ=0 EndX=8 EndY=-27.9096 EndZ=0
    g4: GeomPoint X=69 Y=-13.4548 Z=0
    g5: LineSegment StartX=10.8863 StartY=-4.01261 StartZ=0 EndX=51.5548 EndY=-24.1167 EndZ=0
    g6: LineSegment StartX=50.6685 StartY=-27.9096 StartZ=0 EndX=10 EndY=-27.9096 EndZ=0
    g7: LineSegment StartX=8 StartY=-25.9096 StartZ=0 EndX=8 EndY=-5.8055 EndZ=0
    g8: LineSegment StartX=17.4452 StartY=-2.79289 StartZ=0 EndX=58.1137 EndY=-22.897 EndZ=0
    g9: LineSegment StartX=61 StartY=-21.1041 StartZ=0 EndX=61 EndY=-1 EndZ=0
    g10: LineSegment StartX=59 StartY=1 StartZ=0 EndX=18.3315 EndY=1 EndZ=0
    g11: LineSegment StartX=59.2274 StartY=-27.9096 StartZ=0 EndX=61 EndY=-24.3238 EndZ=0
    g12: LineSegment StartX=8 StartY=-2.58579 StartZ=0 EndX=9.7726 EndY=1 EndZ=0
    g13: ArcOfCircle CenterX=59 CenterY=-21.1041 CenterZ=0 NormalX=0 NormalY=0 NormalZ=1 AngleXU=0 Radius=2 StartAngle=4.25328 EndAngle=6.28319
    g14: GeomPoint X=61 Y=-24.3238 Z=0
    g15: ArcOfCircle CenterX=59 CenterY=-1 CenterZ=0 NormalX=0 NormalY=0 NormalZ=1 AngleXU=0 Radius=2 StartAngle=0 EndAngle=1.5708
    g16: GeomPoint X=61 Y=1 Z=0
    g17: ArcOfCircle CenterX=18.3315 CenterY=-1 CenterZ=0 NormalX=0 NormalY=0 NormalZ=1 AngleXU=0 Radius=2 StartAngle=1.5708 EndAngle=4.25328
    g18: GeomPoint X=9.7726 Y=1 Z=0
    g19: ArcOfCircle CenterX=10 CenterY=-5.8055 CenterZ=0 NormalX=0 NormalY=0 NormalZ=1 AngleXU=0 Radius=2 StartAngle=1.11169 EndAngle=3.14159
    g20: GeomPoint X=8 Y=-2.58579 Z=0
    g21: ArcOfCircle CenterX=10 CenterY=-25.9096 CenterZ=0 NormalX=0 NormalY=0 NormalZ=1 AngleXU=0 Radius=2 StartAngle=3.14159 EndAngle=4.71239
    g22: GeomPoint X=8 Y=-27.9096 Z=0
    g23: ArcOfCircle CenterX=50.6685 CenterY=-25.9096 CenterZ=0 NormalX=0 NormalY=0 NormalZ=1 AngleXU=0 Radius=2 StartAngle=4.71239 EndAngle=7.39487
    g24: GeomPoint X=59.2274 Y=-27.9096 Z=0
    g25: LineSegment StartX=8 StartY=-27.9096 StartZ=0 EndX=8 EndY=-37.9096 EndZ=0
    g26: LineSegment StartX=8 StartY=-37.9096 StartZ=0 EndX=69 EndY=-37.9096 EndZ=0
    g27: LineSegment StartX=61 StartY=-21.1041 StartZ=0 EndX=69 EndY=-21.1041 EndZ=0
    g28: LineSegment StartX=69 StartY=-21.1041 StartZ=0 EndX=69 EndY=-37.9096 EndZ=0
    g29: LineSegment StartX=69 StartY=-37.9096 StartZ=0 EndX=130 EndY=-37.9096 EndZ=0
    g30: LineSegment StartX=130 StartY=-37.9096 StartZ=0 EndX=130 EndY=-27.9096 EndZ=0
  constraints (74):
    c: Coincident(g0,g1)
    c: Coincident(g1,g2)
    c: Coincident(g2,g3)
    c: Coincident(g3,g0)
    c: Horizontal(g1)
    c: Horizontal(g3)
    c: Vertical(g0)
    c: Vertical(g2)
    c: Symmetric(g1,g0,g4)
    c: DistanceY(g-1,g4) = -13.4548
    c: DistanceX(g-1,g0) = 8
    c: DistanceX(g1,g1) = 122
    c: DistanceY(g0,g0) = 28.9096
    c: PointOnObject(g20,g0)
    c: PointOnObject(g24,g3)
    c: Coincident(g22,g0)
    c: PointOnObject(g18,g1)
    c: PointOnObject(g16,g1)
    c: Vertical(g9)
    c: Parallel(g8,g5)
    c: Coincident(g11,g24)
    c: Coincident(g11,g14)
    c: Coincident(g12,g20)
    c: Coincident(g12,g18)
    c: Parallel(g11,g12)
    c: Perpendicular(g5,g11)
    c: Distance(g11) = 4
    c: PointOnObject(g14,g8)
    c: PointOnObject(g14,g9)
    c: Tangent(g8,g13) = -1.5708
    c: Tangent(g9,g13) = -1.5708
    c: PointOnObject(g16,g9)
    c: PointOnObject(g16,g10)
    c: Tangent(g9,g15) = -1.5708
    c: Tangent(g10,g15) = -1.5708
    c: PointOnObject(g18,g10)
    c: PointOnObject(g18,g8)
    c: Tangent(g10,g17) = -1.5708
    c: Tangent(g8,g17) = -1.5708
    c: PointOnObject(g20,g5)
    c: PointOnObject(g20,g7)
    c: Tangent(g5,g19) = 1.5708
    c: Tangent(g7,g19) = 1.5708
    c: PointOnObject(g22,g7)
    c: PointOnObject(g22,g6)
    c: Tangent(g7,g21) = 1.5708
    c: Tangent(g6,g21) = 1.5708
    c: PointOnObject(g24,g6)
    c: PointOnObject(g24,g5)
    c: Tangent(g6,g23) = 1.5708
    c: Tangent(g5,g23) = 1.5708
    c: Equal(g23,g21)
    c: Equal(g21,g19)
    c: Equal(g19,g17)
    c: Equal(g17,g15)
    c: Equal(g15,g13)
    c: Radius(g15) = 2
    c: Coincident(g25,g0)
    c: Vertical(g25)
    c: Coincident(g26,g25)
    c: Horizontal(g26)
    c: DistanceY(g25,g25) = 10
    c: Coincident(g27,g9)
    c: Horizontal(g27)
    c: Coincident(g28,g27)
    c: Coincident(g28,g26)
    c: Vertical(g28)
    c: DistanceX(g27,g27) = 8
    c: Horizontal(g29)
    c: Coincident(g30,g29)
    c: Coincident(g30,g2)
    c: Vertical(g30)
    c: Coincident(g29,g26)
    c: Equal(g26,g29)
FEATURE [PartDesign::Pocket] Pocket  label="TrussCutout"
  BaseFeature = -> Pad
  Direction = (0,0,-1)
  Length = 5
  Length2 = 5
  Midplane = true
  Profile = -> Sketch_1
  ReferenceAxis = -> Sketch_1 [N_Axis]
  Type = 1
FEATURE [PartDesign::LinearPattern] LinearPattern  label="CutoutPattern"
  BaseFeature = -> Pocket
  Direction = -> Sketch_1 [H_Axis]
  Length = 61
  Occurrences = 2
  Originals = -> [Pocket]
  expr: Length = Sketch.Constraints.TrussWidth * 0.5
FEATURE [PartDesign::Body] Body
  Group = -> [Sketch,Pad,Sketch_1,Pocket,LinearPattern]
  Origin = -> Origin001
  Tip = -> LinearPattern
FEATURE [App::Part] Assembly
  AssemblyType = Part::Link
  Group = -> [LCS_Origin,Variables,Constraints,Configurations,Body]
  Origin = -> Origin
  Type = Assembly
---- part BreakawayMagnet.FCStd = doc fcstd_0674e4698032 ----
FCSTD DOCUMENT  (FreeCAD 0.20R29177 +426 (Git))
Label: BreakawayMagnet
License: All rights reserved
LicenseURL: http://en.wikipedia.org/wiki/All_rights_reserved
objects: App::DocumentObjectGroup×3, Sketcher::SketchObject×2, PartDesign::CoordinateSystem×1, App::FeaturePython×1, PartDesign::Revolution×1, PartDesign::Hole×1, PartDesign::Body×1, Part::FeaturePython×1, App::Part×1
note: 9 computed .brp shape members not serialized (recipe doc carries the construction recipe); baked Part::Feature solids carry a one-line shape summary decoded from their .brp

FEATURE [App::DocumentObjectGroup] Parts
FEATURE [PartDesign::CoordinateSystem] LCS_Origin
  AttacherType = Attacher::AttachEngine3D
  MapMode = 2
  Support = -> [X_Axis]
FEATURE [App::FeaturePython] Variables  # WARN: FeaturePython — macro-defined, semantics opaque (R4)
  Type = App::PropertyContainer
FEATURE [App::DocumentObjectGroup] Constraints
FEATURE [App::DocumentObjectGroup] Configurations
FEATURE [Sketcher::SketchObject] Sketch
  FullyConstrained = true
  MapMode = 5
  Placement = pos=(0,0,0) rot=(1,0,0;1.5708rad)
  Support = -> [XZ_Plane001]
  sketch-geometry (8):
    g0: LineSegment StartX=0 StartY=3 StartZ=0 EndX=8.5 EndY=3 EndZ=0
    g1: ArcOfCircle CenterX=8.5 CenterY=2.5 CenterZ=0 NormalX=0 NormalY=0 NormalZ=1 AngleXU=0 Radius=0.5 StartAngle=4.57e-14 EndAngle=1.5708
    g2: LineSegment StartX=9 StartY=2.5 StartZ=0 EndX=9 EndY=0.5 EndZ=0
    g3: ArcOfCircle CenterX=8.5 CenterY=0.5 CenterZ=0 NormalX=0 NormalY=0 NormalZ=1 AngleXU=0 Radius=0.5 StartAngle=4.71239 EndAngle=6.28319
    g4: LineSegment StartX=8.5 StartY=1e-16 StartZ=0 EndX=0 EndY=1e-16 EndZ=0
    g5: LineSegment StartX=0 StartY=1e-16 StartZ=0 EndX=0 EndY=3 EndZ=0
    g6: GeomPoint X=0 Y=3 Z=0
    g7: GeomPoint X=9 Y=0 Z=0
  constraints (19):
    c: Tangent(g0,g1) = 1.5708
    c: Tangent(g1,g2) = 1.5708
    c: Tangent(g2,g3) = 1.5708
    c: Tangent(g3,g4) = 1.5708
    c: Horizontal(g0)
    c: Horizontal(g4)
    c: Vertical(g2)
    c: Vertical(g5)
    c: Equal(g1,g3)
    c: PointOnObject(g6,g0)
    c: PointOnObject(g6,g5)
    c: PointOnObject(g7,g2)
    c: PointOnObject(g7,g4)
    c: Coincident(g5,g4)
    c: Coincident(g5,g0)
    c: Radius(g1) = 0.5
    c: DistanceY(g5,g5) = 3  'Height'
    c: DistanceX(g-1,g1) = 9
    c: Coincident(g4,g-1)
FEATURE [PartDesign::Revolution] Revolution
  Angle = 360
  Axis = (0,2e-16,1)
  Base = (0,0,0)
  Placement = pos=(0,0,0) rot=(1,0,0;1.5708rad)
  Profile = -> Sketch
  ReferenceAxis = -> Sketch [V_Axis]
  Reversed = true
FEATURE [Sketcher::SketchObject] Sketch001
  AttachmentOffset = pos=(0,0,3) rot=(0,0,1;0rad)
  FullyConstrained = true
  MapMode = 5
  Placement = pos=(0,0,3) rot=(0,0,1;0rad)
  Support = -> [XY_Plane001]
  expr: .AttachmentOffset.Base.z = <<Sketch>>.Constraints.Height
  sketch-geometry (1):
    g0: Circle CenterX=0 CenterY=0 CenterZ=0 NormalX=0 NormalY=0 NormalZ=1 AngleXU=0 Radius=1
  constraints (2):
    c: Coincident(g0,g-1)
    c: Diameter(g0) = 2
FEATURE [PartDesign::Hole] Hole  label="MountHole"
  BaseFeature = -> Revolution
  CustomThreadClearance = 0
  Depth = 51.7403
  DepthType = 1
  Diameter = 5.5
  DrillForDepth = false
  DrillPoint = 1
  DrillPointAngle = 118
  HoleCutCountersinkAngle = 90
  HoleCutCustomValues = false
  HoleCutDepth = 3.5
  HoleCutDiameter = 12.2
  HoleCutType = 7
  ModelThread = false
  Placement = pos=(0,0,0) rot=(1,0,0;1.5708rad)
  Profile = -> Sketch001
  Tapered = false
  TaperedAngle = 90
  ThreadClass = 0
  ThreadDepth = 51.7403
  ThreadDepthType = 0
  ThreadDirection = 0
  ThreadFit = 0
  ThreadSize = 13
  ThreadType = 1
  Threaded = false
  UseCustomThreadClearance = false
FEATURE [PartDesign::Body] Body
  Group = -> [Sketch,Revolution,Sketch001,Hole]
  Origin = -> Origin001
  Tip = -> Hole
FEATURE [Part::FeaturePython] Screw  label="M5x16-Screw"  # Fasteners workbench fastener (typed FeaturePython)
  Placement = pos=(0,0,3) rot=(0,0,1;0rad)
  baseObject = -> Sketch001 [Edge1]
  diameter = 5
  invert = false
  leftHanded = false
  length = 3
  lengthCustom = 16
  matchOuter = false
  offset = 0
  thread = false
  type = 18
FEATURE [App::Part] Assembly
  AssemblyType = Part::Link
  Group = -> [LCS_Origin,Variables,Constraints,Configurations,Body,Screw]
  Origin = -> Origin
  Type = Assembly
---- part EndStopTip.FCStd = doc fcstd_322e3f0e3d58 ----
FCSTD DOCUMENT  (FreeCAD 0.20R29177 +426 (Git))
Label: EndStopTip
License: All rights reserved
LicenseURL: http://en.wikipedia.org/wiki/All_rights_reserved
objects: Sketcher::SketchObject×4, App::DocumentObjectGroup×2, PartDesign::Pad×2, PartDesign::Hole×2, PartDesign::Pocket×2, PartDesign::CoordinateSystem×1, App::FeaturePython×1, PartDesign::Body×1, App::Part×1
note: 18 computed .brp shape members not serialized (recipe doc carries the construction recipe); baked Part::Feature solids carry a one-line shape summary decoded from their .brp

FEATURE [PartDesign::CoordinateSystem] LCS_Origin
  AttacherType = Attacher::AttachEngine3D
  MapMode = 2
  Support = -> [X_Axis]
FEATURE [App::FeaturePython] Variables  # WARN: FeaturePython — macro-defined, semantics opaque (R4)
  BaseHeight = 5
  Type = App::PropertyContainer
FEATURE [App::DocumentObjectGroup] Constraints
FEATURE [App::DocumentObjectGroup] Configurations
FEATURE [Sketcher::SketchObject] Sketch
  AttachmentOffset = pos=(0,0,5) rot=(0,0,1;0rad)
  FullyConstrained = true
  MapMode = 5
  Placement = pos=(0,0,5) rot=(0,0,1;0rad)
  Support = -> [XY_Plane001]
  expr: .AttachmentOffset.Base.z = <<Variables>>.BaseHeight
  sketch-geometry (5):
    g0: LineSegment StartX=-20 StartY=-21 StartZ=0 EndX=-20 EndY=21 EndZ=0
    g1: LineSegment StartX=-20 StartY=21 StartZ=0 EndX=20 EndY=21 EndZ=0
    g2: LineSegment StartX=20 StartY=21 StartZ=0 EndX=20 EndY=-21 EndZ=0
    g3: LineSegment StartX=20 StartY=-21 StartZ=0 EndX=-20 EndY=-21 EndZ=0
    g4: GeomPoint X=0 Y=0 Z=0
  constraints (12):
    c: Coincident(g0,g1)
    c: Coincident(g1,g2)
    c: Coincident(g2,g3)
    c: Coincident(g3,g0)
    c: Horizontal(g1)
    c: Horizontal(g3)
    c: Vertical(g0)
    c: Vertical(g2)
    c: Symmetric(g1,g0,g4)
    c: Coincident(g4,g-1)
    c: DistanceX(g3,g3) = 40  'Width'
    c: DistanceY(g2,g2) = 42  'Height'
FEATURE [PartDesign::Pad] Pad
  Direction = (0,0,1)
  Length = 5
  Length2 = 10
  Profile = -> Sketch
  ReferenceAxis = -> Sketch [N_Axis]
  Reversed = true
  Type = 0
  expr: Length = <<Variables>>.BaseHeight
FEATURE [Sketcher::SketchObject] Sketch001
  AttachmentOffset = pos=(0,0,5) rot=(0,0,1;0rad)
  FullyConstrained = true
  MapMode = 5
  Placement = pos=(0,0,5) rot=(0,0,1;0rad)
  Support = -> [XY_Plane001]
  expr: .AttachmentOffset.Base.z = <<Variables>>.BaseHeight
  sketch-geometry (2):
    g0: Circle CenterX=0 CenterY=10 CenterZ=0 NormalX=0 NormalY=0 NormalZ=1 AngleXU=0 Radius=1
    g1: Circle CenterX=0 CenterY=-10 CenterZ=0 NormalX=0 NormalY=0 NormalZ=1 AngleXU=0 Radius=1
  constraints (5):
    c: PointOnObject(g0,g-2)
    c: Equal(g0,g1)
    c: Diameter(g0) = 2
    c: Symmetric(g1,g0,g-1)
    c: DistanceY(g1,g0) = 20
FEATURE [PartDesign::Hole] Hole  label="MountHoles"
  BaseFeature = -> Pad
  CustomThreadClearance = 0
  Depth = 25
  DepthType = 0
  Diameter = 5.5
  DrillForDepth = false
  DrillPoint = 1
  DrillPointAngle = 118
  HoleCutCountersinkAngle = 90
  HoleCutCustomValues = false
  HoleCutDepth = 0
  HoleCutDiameter = 12.2
  HoleCutType = 0
  ModelThread = false
  Profile = -> Sketch001
  Tapered = false
  TaperedAngle = 90
  ThreadClass = 0
  ThreadDepth = 25
  ThreadDepthType = 0
  ThreadDirection = 0
  ThreadFit = 0
  ThreadSize = 13
  ThreadType = 1
  Threaded = false
  UseCustomThreadClearance = false
FEATURE [PartDesign::Pad] Pad001  label="MagnetPad"
  BaseFeature = -> Hole
  Direction = (0,0,1)
  Length = 5
  Length2 = 10
  Profile = -> Sketch
  ReferenceAxis = -> Sketch [N_Axis]
  Type = 0
FEATURE [PartDesign::Hole] Hole001  label="MagnetHoles"
  BaseFeature = -> Pad001
  CustomThreadClearance = 0
  Depth = 25
  DepthType = 0
  Diameter = 18.6
  DrillForDepth = false
  DrillPoint = 1
  DrillPointAngle = 118
  HoleCutCountersinkAngle = 90
  HoleCutCustomValues = false
  HoleCutDepth = 0
  HoleCutDiameter = 0
  HoleCutType = 0
  ModelThread = false
  Profile = -> Sketch001
  Reversed = true
  Tapered = false
  TaperedAngle = 90
  ThreadClass = 0
  ThreadDepth = 25
  ThreadDepthType = 0
  ThreadDirection = 0
  ThreadFit = 0
  ThreadSize = 0
  ThreadType = 0
  Threaded = false
  UseCustomThreadClearance = false
FEATURE [Sketcher::SketchObject] Sketch002
  FullyConstrained = true
  MapMode = 5
  Support = -> [XY_Plane001]
  expr: Constraints[21] = <<Sketch>>.Constraints.Height
  expr: Constraints[22] = <<Sketch>>.Constraints.Width
  sketch-geometry (15):
    g0: ArcOfCircle CenterX=-17 CenterY=18 CenterZ=0 NormalX=0 NormalY=0 NormalZ=1 AngleXU=0 Radius=3 StartAngle=1.5708 EndAngle=3.14159
    g1: LineSegment StartX=-17 StartY=21 StartZ=0 EndX=17 EndY=21 EndZ=0
    g2: ArcOfCircle CenterX=17 CenterY=18 CenterZ=0 NormalX=0 NormalY=0 NormalZ=1 AngleXU=0 Radius=3 StartAngle=3e-16 EndAngle=1.5708
    g3: LineSegment StartX=20 StartY=18 StartZ=0 EndX=20 EndY=-18 EndZ=0
    g4: ArcOfCircle CenterX=17 CenterY=-18 CenterZ=0 NormalX=0 NormalY=0 NormalZ=1 AngleXU=0 Radius=3 StartAngle=4.71239 EndAngle=6.28319
    g5: LineSegment StartX=17 StartY=-21 StartZ=0 EndX=-17 EndY=-21 EndZ=0
    g6: ArcOfCircle CenterX=-17 CenterY=-18 CenterZ=0 NormalX=0 NormalY=0 NormalZ=1 AngleXU=0 Radius=3 StartAngle=3.14159 EndAngle=4.71239
    g7: LineSegment StartX=-20 StartY=-18 StartZ=0 EndX=-20 EndY=18 EndZ=0
    g8: GeomPoint X=-20 Y=21 Z=0
    g9: GeomPoint X=20 Y=-21 Z=0
    g10: LineSegment StartX=-41 StartY=-41 StartZ=0 EndX=-41 EndY=41 EndZ=0
    g11: LineSegment StartX=-41 StartY=41 StartZ=0 EndX=41 EndY=41 EndZ=0
    g12: LineSegment StartX=41 StartY=41 StartZ=0 EndX=41 EndY=-41 EndZ=0
    g13: LineSegment StartX=41 StartY=-41 StartZ=0 EndX=-41 EndY=-41 EndZ=0
    g14: GeomPoint X=0 Y=0 Z=0
  constraints (35):
    c: Tangent(g0,g1) = 1.5708
    c: Tangent(g1,g2) = 1.5708
    c: Tangent(g2,g3) = 1.5708
    c: Tangent(g3,g4) = 1.5708
    c: Tangent(g4,g5) = 1.5708
    c: Tangent(g5,g6) = 1.5708
    c: Tangent(g6,g7) = 1.5708
    c: Tangent(g7,g0) = 1.5708
    c: Horizontal(g1)
    c: Horizontal(g5)
    c: Vertical(g3)
    c: Vertical(g7)
    c: Equal(g0,g2)
    c: Equal(g2,g4)
    c: Equal(g4,g6)
    c: PointOnObject(g8,g1)
    c: PointOnObject(g8,g7)
    c: PointOnObject(g9,g3)
    c: PointOnObject(g9,g5)
    c: Symmetric(g4,g0,g-1)
    c: Radius(g4) = 3
    c: DistanceY(g4,g1) = 42
    c: DistanceX(g0,g2) = 40
    c: Coincident(g10,g11)
    c: Coincident(g11,g12)
    c: Coincident(g12,g13)
    c: Coincident(g13,g10)
    c: Horizontal(g11)
    c: Horizontal(g13)
    c: Vertical(g10)
    c: Vertical(g12)
    c: Symmetric(g11,g10,g14)
    c: Coincident(g14,g-1)
    c: Equal(g12,g11)
    c: DistanceY(g1,g11) = 20
FEATURE [PartDesign::Pocket] Pocket  label="CornerFillets"
  BaseFeature = -> Hole001
  Direction = (0,0,-1)
  Length = 5
  Length2 = 5
  Midplane = true
  Profile = -> Sketch002
  ReferenceAxis = -> Sketch002 [N_Axis]
  Type = 1
FEATURE [Sketcher::SketchObject] Sketch003  label="SketchChamfer"
  FullyConstrained = true
  MapMode = 5
  Placement = pos=(0,0,0) rot=(1,0,0;1.5708rad)
  Support = -> [XZ_Plane001]
  expr: Constraints[26] = <<Pad>>.Length + <<MagnetPad>>.Length
  expr: Constraints[9] = <<Sketch>>.Constraints.Width
  sketch-geometry (10):
    g0: LineSegment StartX=11 StartY=10 StartZ=0 EndX=20 EndY=2 EndZ=0
    g1: LineSegment StartX=20 StartY=2 StartZ=0 EndX=-20 EndY=2 EndZ=0
    g2: LineSegment StartX=-20 StartY=2 StartZ=0 EndX=-11 EndY=10 EndZ=0
    g3: LineSegment StartX=-11 StartY=10 StartZ=0 EndX=11 EndY=10 EndZ=0
    g4: GeomPoint X=0 Y=2 Z=0
    g5: LineSegment StartX=-20 StartY=2 StartZ=0 EndX=-21 EndY=2 EndZ=0
    g6: LineSegment StartX=-21 StartY=2 StartZ=0 EndX=-21 EndY=11 EndZ=0
    g7: LineSegment StartX=-21 StartY=11 StartZ=0 EndX=21 EndY=11 EndZ=0
    g8: LineSegment StartX=21 StartY=11 StartZ=0 EndX=21 EndY=2 EndZ=0
    g9: LineSegment StartX=21 StartY=2 StartZ=0 EndX=20 EndY=2 EndZ=0
  constraints (27):
    c: Coincident(g0,g1)
    c: Coincident(g1,g2)
    c: Coincident(g2,g3)
    c: Coincident(g3,g0)
    c: Horizontal(g1)
    c: Horizontal(g3)
    c: PointOnObject(g4,g-2)
    c: Equal(g0,g2)
    c: Symmetric(g0,g1,g4)
    c: DistanceX(g1,g1) = 40
    c: DistanceX(g3,g3) = 22  'MateWidth'
    c: DistanceY(g-1,g4) = 2
    c: Coincident(g5,g2)
    c: Horizontal(g5)
    c: Coincident(g6,g5)
    c: Vertical(g6)
    c: Coincident(g6,g7)
    c: Horizontal(g7)
    c: Coincident(g7,g8)
    c: Vertical(g8)
    c: Coincident(g8,g9)
    c: Coincident(g9,g0)
    c: Horizontal(g9)
    c: Equal(g9,g5)
    c: DistanceX(g9,g9) = 1
    c: DistanceY(g0,g7) = 1
    c: DistanceY(g-1,g0) = 10
FEATURE [PartDesign::Pocket] Pocket001  label="Chamfer"
  BaseFeature = -> Pocket
  Direction = (0,1,2e-16)
  Length = 5
  Length2 = 5
  Midplane = true
  Profile = -> Sketch003
  ReferenceAxis = -> Sketch003 [N_Axis]
  Type = 1
FEATURE [PartDesign::Body] Body
  Group = -> [Sketch,Pad,Sketch001,Hole,Pad001,Hole001,Sketch002,Pocket,Sketch003,Pocket001]
  Origin = -> Origin001
  Tip = -> Pocket001
FEATURE [App::Part] Assembly
  AssemblyType = Part::Link
  Group = -> [LCS_Origin,Variables,Constraints,Configurations,Body]
  Origin = -> Origin
  Type = Assembly
---- part HeadTetherMountClip.FCStd = doc fcstd_fd857a80e36b ----
FCSTD DOCUMENT  (FreeCAD 0.20R29177 +426 (Git))
Label: HeadTetherMountClip
License: All rights reserved
LicenseURL: http://en.wikipedia.org/wiki/All_rights_reserved
objects: App::DocumentObjectGroup×4, Part::FeaturePython×4, PartDesign::CoordinateSystem×1, App::FeaturePython×1, Sketcher::SketchObject×1, PartDesign::Pad×1, PartDesign::Body×1, App::Part×1
note: 9 computed .brp shape members not serialized (recipe doc carries the construction recipe); baked Part::Feature solids carry a one-line shape summary decoded from their .brp

FEATURE [App::DocumentObjectGroup] Parts
FEATURE [PartDesign::CoordinateSystem] LCS_Origin
  AttacherType = Attacher::AttachEngine3D
  MapMode = 2
  Support = -> [X_Axis]
FEATURE [App::FeaturePython] Variables  # WARN: FeaturePython — macro-defined, semantics opaque (R4)
  Type = App::PropertyContainer
FEATURE [App::DocumentObjectGroup] Constraints
FEATURE [App::DocumentObjectGroup] Configurations
FEATURE [Sketcher::SketchObject] Sketch
  FullyConstrained = true
  MapMode = 5
  Support = -> [XY_Plane001]
  sketch-geometry (21):
    g0: Circle CenterX=-8 CenterY=0 CenterZ=0 NormalX=0 NormalY=0 NormalZ=1 AngleXU=0 Radius=2.7
    g1: Circle CenterX=0 CenterY=-16 CenterZ=0 NormalX=0 NormalY=0 NormalZ=1 AngleXU=0 Radius=3
    g2: ArcOfCircle CenterX=0 CenterY=-16 CenterZ=0 NormalX=0 NormalY=0 NormalZ=1 AngleXU=0 Radius=6 StartAngle=3.94927 EndAngle=5.4755
    g3: LineSegment StartX=-13.5294 StartY=-11.3629 StartZ=0 EndX=-4.14705 EndY=-20.3361 EndZ=0
    g4: LineSegment StartX=4.14705 StartY=-20.3361 StartZ=0 EndX=13.5294 EndY=-11.3629 EndZ=0
    g5: LineSegment StartX=-16 StartY=-5.58137 StartZ=0 EndX=-16 EndY=7.5 EndZ=0
    g6: LineSegment StartX=16 StartY=-5.58137 StartZ=0 EndX=16 EndY=7.5 EndZ=0
    g7: LineSegment StartX=-14.5 StartY=9 StartZ=0 EndX=14.5 EndY=9 EndZ=0
    g8: ArcOfCircle CenterX=-14.5 CenterY=7.5 CenterZ=0 NormalX=0 NormalY=0 NormalZ=1 AngleXU=0 Radius=1.5 StartAngle=1.5708 EndAngle=3.14159
    g9: GeomPoint X=-16 Y=9 Z=0
    g10: ArcOfCircle CenterX=14.5 CenterY=7.5 CenterZ=0 NormalX=0 NormalY=0 NormalZ=1 AngleXU=0 Radius=1.5 StartAngle=0 EndAngle=1.5708
    g11: GeomPoint X=16 Y=9 Z=0
    g12: GeomPoint X=0 Y=9 Z=0
    g13: ArcOfCircle CenterX=8 CenterY=-5.58137 CenterZ=0 NormalX=0 NormalY=0 NormalZ=1 AngleXU=0 Radius=8 StartAngle=5.4755 EndAngle=6.28319
    g14: GeomPoint X=16 Y=-9 Z=0
    g15: ArcOfCircle CenterX=-8 CenterY=-5.58137 CenterZ=0 NormalX=0 NormalY=0 NormalZ=1 AngleXU=0 Radius=8 StartAngle=3.14159 EndAngle=3.94927
    g16: GeomPoint X=-16 Y=-9 Z=0
    g17: LineSegment StartX=-16 StartY=-9 StartZ=0 EndX=16 EndY=-9 EndZ=0
    g18: Circle CenterX=8 CenterY=0 CenterZ=0 NormalX=0 NormalY=0 NormalZ=1 AngleXU=0 Radius=2.7
    g19: LineSegment StartX=-8 StartY=0 StartZ=0 EndX=8 EndY=0 EndZ=0
    g20: LineSegment StartX=0 StartY=9 StartZ=0 EndX=0 EndY=-9 EndZ=0
  constraints (47):
    c: PointOnObject(g1,g-2)
    c: Tangent(g3,g2) = -1.5708
    c: Tangent(g2,g4) = -1.5708
    c: Coincident(g2,g1)
    c: Diameter(g1) = 6
    c: Diameter(g0) = 5.4
    c: DistanceY(g1,g0) = 16
    c: Radius(g2) = 6
    c: Vertical(g5)
    c: Vertical(g6)
    c: Horizontal(g7)
    c: PointOnObject(g9,g7)
    c: PointOnObject(g9,g5)
    c: Tangent(g7,g8) = 1.5708
    c: Tangent(g5,g8) = 1.5708
    c: PointOnObject(g11,g7)
    c: PointOnObject(g11,g6)
    c: Tangent(g7,g10) = 1.5708
    c: Tangent(g6,g10) = -1.5708
    c: Equal(g10,g8)
    c: Radius(g10) = 1.5
    c: PointOnObject(g12,g-2)
    c: Symmetric(g7,g7,g12)
    c: PointOnObject(g14,g4)
    c: PointOnObject(g14,g6)
    c: Tangent(g4,g13) = -1.5708
    c: Tangent(g6,g13) = -1.5708
    c: PointOnObject(g16,g3)
    c: PointOnObject(g16,g5)
    c: Tangent(g3,g15) = -1.5708
    c: Tangent(g5,g15) = 1.5708
    c: Equal(g13,g15)
    c: Radius(g13) = 8
    c: Equal(g3,g4)
    c: Coincident(g17,g16)
    c: Coincident(g17,g14)
    c: DistanceY(g14,g7) = 18
    c: PointOnObject(g0,g-1)
    c: Equal(g18,g0)
    c: Coincident(g19,g0)
    c: Coincident(g19,g18)
    c: Symmetric(g18,g0,g-1)
    c: Coincident(g20,g12)
    c: PointOnObject(g20,g17)
    c: Symmetric(g20,g12,g-1)
    c: DistanceX(g19,g19) = 16  'MountHoleSpacing'
    c: DistanceX(g18,g6) = 8
FEATURE [PartDesign::Pad] Pad
  Direction = (0,0,1)
  Length = 3
  Length2 = 10
  Profile = -> Sketch
  ReferenceAxis = -> Sketch [N_Axis]
  Type = 0
FEATURE [PartDesign::Body] Body
  Group = -> [Sketch,Pad]
  Origin = -> Origin001
  Tip = -> Pad
FEATURE [Part::FeaturePython] Washer  label="M5-Washer"  # Fasteners workbench fastener (typed FeaturePython)
  Placement = pos=(-8,0,3) rot=(0,0,1;0rad)
  baseObject = -> Sketch [Edge1]
  diameter = 6
  invert = false
  matchOuter = false
  offset = 3
  type = 3
  expr: offset = <<Pad>>.Length
FEATURE [Part::FeaturePython] Screw  label="M5x10-Screw"  # Fasteners workbench fastener (typed FeaturePython)
  Placement = pos=(-8,0,4.1) rot=(0,0,1;0rad)
  baseObject = -> Washer [Edge1]
  diameter = 3
  invert = false
  leftHanded = false
  length = 1
  lengthCustom = 10
  matchOuter = false
  offset = 0
  thread = false
  type = 40
FEATURE [App::DocumentObjectGroup] Fasteners
  Group = -> [Washer,Screw]
FEATURE [Part::FeaturePython] Array_Washer  label="Array_M5-Washer"  # Draft array (typed FeaturePython)
  ArraySteps = 0
  ArrayType = Circular Array
  Axis = LCS_Origin.Z
  Count = 2
  ElementCount = 2
  FullAngle = 360
  IntervalAngle = 180
  LinearSteps = 0
  PlacementList = 2 placements: [(-8,0,3),(8,-9.79717e-16,3)]
  ScaleList = (2) [(1,1,1),(1,1,1)]
  ShowElement = false
  SourceObject = -> Washer
FEATURE [Part::FeaturePython] Array_Screw  label="Array_M5x10-Screw"  # Draft array (typed FeaturePython)
  ArraySteps = 0
  ArrayType = Circular Array
  Axis = LCS_Origin.Z
  Count = 2
  ElementCount = 2
  FullAngle = 360
  IntervalAngle = 180
  LinearSteps = 0
  PlacementList = 2 placements: [(-8,0,4.1),(8,-9.79717e-16,4.1)]
  ScaleList = (2) [(1,1,1),(1,1,1)]
  ShowElement = false
  SourceObject = -> Screw
FEATURE [App::Part] Assembly
  AssemblyType = Part::Link
  Group = -> [LCS_Origin,Variables,Constraints,Configurations,Body,Fasteners,Washer,Screw,Array_Washer,Array_Screw]
  Origin = -> Origin
  Type = Assembly
